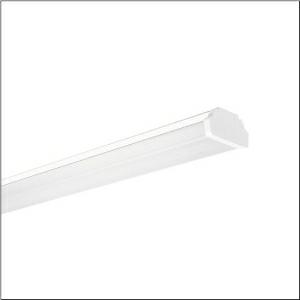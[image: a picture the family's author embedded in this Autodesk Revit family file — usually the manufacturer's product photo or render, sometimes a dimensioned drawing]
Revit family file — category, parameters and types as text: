
# Revit family: dus_r__31_gen_2_53bd812mv4a5c2_5567
name_source: partatom
category: Lighting Fixtures
units: mm (PartAtom-declared; Revit-internal decimal feet)

## family parameters
Cut with Voids When Loaded = No
Host = Face
Light Source = No
Part Type = Normal
Room Calculation Point = No
Round Connector Dimension = Use Diameter
Shared = No

## types (1)
- --- (1 x LED, 10960 lm, 60.5 W, 4000K)
    Apparent Load = 61 VA
    CIE Flux Codes = 47 80 95 93 100
    Color Rendering = 80
    Color Temperature = 4000K
    Default Elevation = 1800 mm
    Description = DUS® 31 Gen.2, luminaire insert, of sheet steel, coil coated, white, length: 1.535mm, width: 81mm, height: 90mm, 5x system unit, system units: 307mm, LED rated luminous flux: 10.960lm, light colour: 840, control gear: ON/OFF Multilumen, control gear: ECG, with plug, 3-pole, with phase selection, mains connection: 220..240V, AC, 50/60Hz, rated input power: 61W, through-wiring accessed according to module size, primary optical cover: cover, of PMMA, light emission: direct distribution, primary light characteristic: symmetric, protection rating (complete): IP20, protection rating (LED compartment): IP50, insulation class (complete): insulation class I (protective earthing), certification: CE, ENEC, VDE, UKCA, impact resistance: IK03, permissible ambient temperature for indoor applications: -35..+40°C, corresponds to IFS (International Featured Standards) requirements for safety and quality in the food industry, reducing of maximum allowable ambient temperature of 5°C with ceiling mounting, packaging unit: 1 piece
    Height = 95 mm
    Lamp = 1 x LED
    Lamp Light Flux = 10960 lm
    Lamp Power = 60.5 W
    Lamp count = 1
    Length = 1535 mm
    Luminous efficacy = 181 lm/W
    Manufacturer = Siteco
    ModVariant = No
    Model = 53BD812MV4A5C2
    Mounting Place = Ceiling
    Mounting Type = Pendant
    Number of Poles = 1
    OnlyDefault = Yes
    Power Factor = 1
    Product Name = DUS® 31 Gen.2
    Product group = luminaire insert | ceiling pendant
    ProductGroupID = 902
    Protection Class = Protection class I
    Protection Degree = IP 20
    RLX_Detail_Level = 1
    RLX_Emergency_Light_Flux = 0 lm
    RLX_Emergency_Type = 0
    RLX_Emergency_Type_DB = No
    RlxData = <blob elided: 29729 chars, md5=64c945c8>
    Socket = socket
    Standby Power = 0 W
    System Light Flux = 10960 lm
    System Power = 61 W
    Type Comments = factory setting: luminous flux: 100 % | (A | C | E) | 140 mA
    Type Image = l_1319596.jpg
    URL = http://relux.com
    VarID = @adj_063123
    Voltage = 0 V
    Weight = 0.00 kg
    Width = 81 mm

## geometry (parser evidence)
native form markers: Blend x4, Sweep x10
no freeform markers — native parametric forms only
